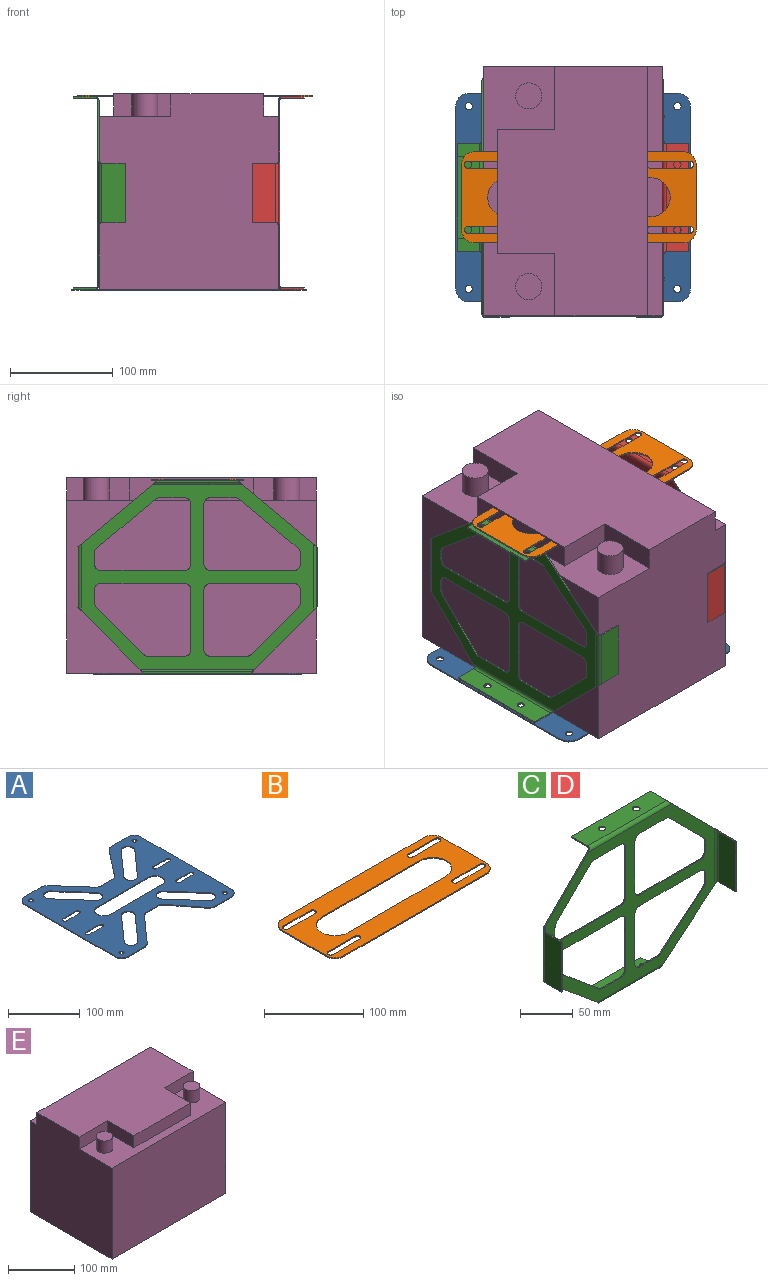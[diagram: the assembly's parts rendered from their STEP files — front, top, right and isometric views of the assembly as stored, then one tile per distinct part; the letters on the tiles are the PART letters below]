
ASSEMBLY  parts=5 mates=12
PART A: 66 faces, bbox 228.6x203.2x1.3 mm
  f0: plane 228.6x203.2mm, normal (0,0,1), area 27129.1mm2, adj f2,f3,f4,f5,f6,f7,f8,f9
  f1: plane 228.6x203.2mm, normal (0,0,-1), area 27129.1mm2, adj f2,f3,f4,f5,f6,f7,f8,f9
  f2: plane 31.89x1.27mm, normal (0,1,0), area 40.5mm2, adj f0,f1,f40,f45
  f3: plane 31.89x1.27mm, normal (0,-1,0), area 40.5mm2, adj f0,f1,f37,f44
  f4: plane 32.4x1.27mm, normal (0,1,0), area 41.1mm2, adj f0,f1,f39,f42
  f5: plane 177.8x1.27mm, normal (-1,0,0), area 225.8mm2, adj f0,f1,f42,f43
  f6: plane 32.4x1.27mm, normal (0,-1,0), area 41.1mm2, adj f0,f1,f36,f43
  f7: plane 177.8x1.27mm, normal (1,0,0), area 225.8mm2, adj f0,f1,f44,f45
  f8: cylinder r=3.57mm len=7.14mm, axis (0,0,1), area 14.2mm2, adj f0,f1,f9,f11
  f9: plane 25.4x1.27mm, normal (0,1,0), area 32.3mm2, adj f0,f1,f8,f10
  f10: cylinder r=3.57mm len=7.14mm, axis (0,0,1), area 14.2mm2, adj f0,f1,f9,f11
  f11: plane 25.4x1.27mm, normal (0,-1,0), area 32.3mm2, adj f0,f1,f8,f10
  f12: cylinder r=3.57mm len=7.14mm, axis (0,0,1), area 28.5mm2, adj f0,f1
  f13: cylinder r=3.57mm len=7.14mm, axis (0,0,1), area 28.5mm2, adj f0,f1
  f14: cylinder r=3.57mm len=7.14mm, axis (0,0,1), area 28.5mm2, adj f0,f1
  f15: cylinder r=3.57mm len=7.14mm, axis (0,0,1), area 14.2mm2, adj f0,f1,f16,f18
  f16: plane 25.4x1.27mm, normal (0,-1,0), area 32.3mm2, adj f0,f1,f15,f17
  f17: cylinder r=3.57mm len=7.14mm, axis (0,0,1), area 14.2mm2, adj f0,f1,f16,f18
  f18: plane 25.4x1.27mm, normal (0,1,0), area 32.3mm2, adj f0,f1,f15,f17
  f19: cylinder r=3.57mm len=7.14mm, axis (0,0,1), area 14.2mm2, adj f0,f1,f20,f22
  f20: plane 25.4x1.27mm, normal (0,1,0), area 32.3mm2, adj f0,f1,f19,f21
  f21: cylinder r=3.57mm len=7.14mm, axis (0,0,1), area 14.2mm2, adj f0,f1,f20,f22
  f22: plane 25.4x1.27mm, normal (0,-1,0), area 32.3mm2, adj f0,f1,f19,f21
  f23: plane 25.4x1.27mm, normal (0,1,0), area 32.3mm2, adj f0,f1,f24,f26
  f24: cylinder r=3.57mm len=7.14mm, axis (0,0,1), area 14.2mm2, adj f0,f1,f23,f25
  f25: plane 25.4x1.27mm, normal (0,-1,0), area 32.3mm2, adj f0,f1,f24,f26
  f26: cylinder r=3.57mm len=7.14mm, axis (0,0,1), area 14.2mm2, adj f0,f1,f23,f25
  f27: cylinder r=3.57mm len=7.14mm, axis (0,0,1), area 28.5mm2, adj f0,f1
  f28: plane 47.34x36.82mm, normal (-0.79,-0.61,0), area 76.2mm2, adj f0,f1,f34,f37
  f29: plane 19.84x1.27mm, normal (0,-1,0), area 25.2mm2, adj f0,f1,f34,f35
  f30: plane 48.63x43.22mm, normal (0.75,-0.66,0), area 82.6mm2, adj f0,f1,f35,f36
  f31: plane 19.84x1.27mm, normal (0,1,0), area 25.2mm2, adj f0,f1,f38,f41
  f32: plane 47.34x36.82mm, normal (-0.79,0.61,0), area 76.2mm2, adj f0,f1,f40,f41
  f33: plane 48.63x43.22mm, normal (0.75,0.66,0), area 82.6mm2, adj f0,f1,f38,f39
  f34: cylinder r=12.7mm len=10.02mm, axis (0,0,-1), area 14.7mm2, adj f0,f1,f28,f29
  f35: cylinder r=12.7mm len=9.49mm, axis (0,0,1), area 13.6mm2, adj f0,f1,f29,f30
  f36: cylinder r=12.7mm len=9.49mm, axis (0,0,1), area 13.6mm2, adj f0,f1,f6,f30
  f37: cylinder r=12.7mm len=10.02mm, axis (0,0,-1), area 14.7mm2, adj f0,f1,f3,f28
  f38: cylinder r=12.7mm len=9.49mm, axis (0,0,1), area 13.6mm2, adj f0,f1,f31,f33
  f39: cylinder r=12.7mm len=9.49mm, axis (0,0,1), area 13.6mm2, adj f0,f1,f4,f33
  f40: cylinder r=12.7mm len=10.02mm, axis (0,0,-1), area 14.7mm2, adj f0,f1,f2,f32
  f41: cylinder r=12.7mm len=10.02mm, axis (0,0,-1), area 14.7mm2, adj f0,f1,f31,f32
  f42: cylinder r=12.7mm len=12.7mm, axis (0,0,-1), area 25.3mm2, adj f0,f1,f4,f5
  f43: cylinder r=12.7mm len=12.7mm, axis (0,0,1), area 25.3mm2, adj f0,f1,f5,f6
  f44: cylinder r=12.7mm len=12.7mm, axis (0,0,-1), area 25.3mm2, adj f0,f1,f3,f7
  f45: cylinder r=12.7mm len=12.7mm, axis (0,0,1), area 25.3mm2, adj f0,f1,f2,f7
  f46: plane 47.46x42.19mm, normal (0.75,0.66,0), area 80.6mm2, adj f0,f1,f47,f49
  f47: cylinder r=9.53mm len=16.64mm, axis (0,0,1), area 38mm2, adj f0,f1,f46,f48
  f48: plane 47.46x42.19mm, normal (-0.75,-0.66,0), area 80.6mm2, adj f0,f1,f47,f49
  f49: cylinder r=9.53mm len=16.64mm, axis (0,0,1), area 38mm2, adj f0,f1,f46,f48
  f50: cylinder r=12.7mm len=25.4mm, axis (0,0,1), area 50.7mm2, adj f0,f1,f51,f53
  f51: plane 101.6x1.27mm, normal (0,-1,0), area 129mm2, adj f0,f1,f50,f52
  f52: cylinder r=12.7mm len=25.4mm, axis (0,0,1), area 50.7mm2, adj f0,f1,f51,f53
  f53: plane 101.6x1.27mm, normal (0,1,0), area 129mm2, adj f0,f1,f50,f52
  f54: plane 47.46x42.19mm, normal (0.75,0.66,0), area 80.6mm2, adj f0,f1,f55,f57
  f55: cylinder r=9.53mm len=16.64mm, axis (0,0,1), area 38mm2, adj f0,f1,f54,f56
  f56: plane 47.46x42.19mm, normal (-0.75,-0.66,0), area 80.6mm2, adj f0,f1,f55,f57
  f57: cylinder r=9.53mm len=16.64mm, axis (0,0,1), area 38mm2, adj f0,f1,f54,f56
  f58: cylinder r=9.53mm len=16.64mm, axis (0,0,1), area 38mm2, adj f0,f1,f59,f61
  f59: plane 47.46x42.19mm, normal (0.75,-0.66,0), area 80.6mm2, adj f0,f1,f58,f60
  f60: cylinder r=9.53mm len=16.64mm, axis (0,0,1), area 38mm2, adj f0,f1,f59,f61
  f61: plane 47.46x42.19mm, normal (-0.75,0.66,0), area 80.6mm2, adj f0,f1,f58,f60
  f62: cylinder r=9.53mm len=16.64mm, axis (0,0,1), area 38mm2, adj f0,f1,f63,f65
  f63: plane 47.46x42.19mm, normal (-0.75,0.66,0), area 80.6mm2, adj f0,f1,f62,f64
  f64: cylinder r=9.53mm len=16.64mm, axis (0,0,1), area 38mm2, adj f0,f1,f63,f65
  f65: plane 47.46x42.19mm, normal (0.75,-0.66,0), area 80.6mm2, adj f0,f1,f62,f64
PART B: 30 faces, bbox 228.6x88.9x1.3 mm
  f0: plane 228.6x88.9mm, normal (0,0,1), area 12473.6mm2, adj f2,f3,f4,f5,f6,f7,f8,f9
  f1: plane 228.6x88.9mm, normal (0,0,-1), area 12473.6mm2, adj f2,f3,f4,f5,f6,f7,f8,f9
  f2: plane 203.2x1.27mm, normal (0,1,0), area 258.1mm2, adj f0,f1,f6,f9
  f3: plane 63.5x1.27mm, normal (-1,0,0), area 80.6mm2, adj f0,f1,f6,f7
  f4: plane 203.2x1.27mm, normal (0,-1,0), area 258.1mm2, adj f0,f1,f7,f8
  f5: plane 63.5x1.27mm, normal (1,0,0), area 80.6mm2, adj f0,f1,f8,f9
  f6: cylinder r=12.7mm len=12.7mm, axis (0,0,-1), area 25.3mm2, adj f0,f1,f2,f3
  f7: cylinder r=12.7mm len=12.7mm, axis (0,0,1), area 25.3mm2, adj f0,f1,f3,f4
  f8: cylinder r=12.7mm len=12.7mm, axis (0,0,-1), area 25.3mm2, adj f0,f1,f4,f5
  f9: cylinder r=12.7mm len=12.7mm, axis (0,0,1), area 25.3mm2, adj f0,f1,f2,f5
  f10: cylinder r=3.57mm len=7.14mm, axis (0,0,1), area 14.2mm2, adj f0,f1,f11,f13
  f11: plane 38.1x1.27mm, normal (0,1,0), area 48.4mm2, adj f0,f1,f10,f12
  f12: cylinder r=3.57mm len=7.14mm, axis (0,0,1), area 14.2mm2, adj f0,f1,f11,f13
  f13: plane 38.1x1.27mm, normal (0,-1,0), area 48.4mm2, adj f0,f1,f10,f12
  f14: plane 38.1x1.27mm, normal (0,-1,0), area 48.4mm2, adj f0,f1,f15,f17
  f15: cylinder r=3.57mm len=7.14mm, axis (0,0,1), area 14.2mm2, adj f0,f1,f14,f16
  f16: plane 38.1x1.27mm, normal (0,1,0), area 48.4mm2, adj f0,f1,f15,f17
  f17: cylinder r=3.57mm len=7.14mm, axis (0,0,1), area 14.2mm2, adj f0,f1,f14,f16
  f18: plane 38.1x1.27mm, normal (0,1,0), area 48.4mm2, adj f0,f1,f19,f21
  f19: cylinder r=3.57mm len=7.14mm, axis (0,0,1), area 14.2mm2, adj f0,f1,f18,f20
  f20: plane 38.1x1.27mm, normal (0,-1,0), area 48.4mm2, adj f0,f1,f19,f21
  f21: cylinder r=3.57mm len=7.14mm, axis (0,0,1), area 14.2mm2, adj f0,f1,f18,f20
  f22: plane 38.1x1.27mm, normal (0,-1,0), area 48.4mm2, adj f0,f1,f23,f25
  f23: cylinder r=3.57mm len=7.14mm, axis (0,0,1), area 14.2mm2, adj f0,f1,f22,f24
  f24: plane 38.1x1.27mm, normal (0,1,0), area 48.4mm2, adj f0,f1,f23,f25
  f25: cylinder r=3.57mm len=7.14mm, axis (0,0,1), area 14.2mm2, adj f0,f1,f22,f24
  f26: cylinder r=19.05mm len=38.1mm, axis (0,0,1), area 76mm2, adj f0,f1,f27,f29
  f27: plane 139.7x1.27mm, normal (0,-1,0), area 177.4mm2, adj f0,f1,f26,f28
  f28: cylinder r=19.05mm len=38.1mm, axis (0,0,1), area 76mm2, adj f0,f1,f27,f29
  f29: plane 139.7x1.27mm, normal (0,1,0), area 177.4mm2, adj f0,f1,f26,f28
PART C: 86 faces, bbox 233.7x50.8x187.3 mm
  f0: plane 57.15x57.15mm, normal (-0.71,0,0.71), area 102.6mm2, adj f44,f45,f60,f83
  f1: plane 69.34x57.79mm, normal (-0.64,0,-0.77), area 114.6mm2, adj f44,f45,f61,f71
  f2: plane 69.34x57.79mm, normal (0.64,0,-0.77), area 114.6mm2, adj f44,f45,f52,f72
  f3: cylinder r=6.35mm len=4.49mm, axis (0,-1,0), area 6.3mm2, adj f4,f42,f44,f45
  f4: plane 45.99x45.99mm, normal (0.71,0,-0.71), area 82.6mm2, adj f3,f5,f44,f45
  f5: cylinder r=6.35mm len=4.49mm, axis (0,-1,0), area 6.3mm2, adj f4,f6,f44,f45
  f6: plane 35.29x1.27mm, normal (0,0,-1), area 44.8mm2, adj f5,f7,f44,f45
  f7: cylinder r=6.35mm len=6.35mm, axis (0,-1,0), area 12.7mm2, adj f6,f8,f44,f45
  f8: plane 58.1x1.27mm, normal (-1,0,0), area 73.8mm2, adj f7,f9,f44,f45
  f9: cylinder r=6.35mm len=6.35mm, axis (0,-1,0), area 12.7mm2, adj f8,f10,f44,f45
  f10: plane 81.28x1.27mm, normal (0,0,1), area 103.2mm2, adj f9,f11,f44,f45
  f11: cylinder r=6.35mm len=6.35mm, axis (0,-1,0), area 12.7mm2, adj f10,f42,f44,f45
  f12: cylinder r=6.35mm len=6.35mm, axis (0,-1,0), area 12.7mm2, adj f13,f41,f44,f45
  f13: plane 35.29x1.27mm, normal (0,0,-1), area 44.8mm2, adj f12,f14,f44,f45
  f14: cylinder r=6.35mm len=4.49mm, axis (0,-1,0), area 6.3mm2, adj f13,f15,f44,f45
  f15: plane 45.99x45.99mm, normal (-0.71,0,-0.71), area 82.6mm2, adj f14,f16,f44,f45
  f16: cylinder r=6.35mm len=4.49mm, axis (0,-1,0), area 6.3mm2, adj f15,f17,f44,f45
  f17: plane 12.11x1.27mm, normal (-1,0,0), area 15.4mm2, adj f16,f18,f44,f45
  f18: cylinder r=6.35mm len=6.35mm, axis (0,-1,0), area 12.7mm2, adj f17,f19,f44,f45
  f19: plane 81.28x1.27mm, normal (0,0,1), area 103.2mm2, adj f18,f20,f44,f45
  f20: cylinder r=6.35mm len=6.35mm, axis (0,-1,0), area 12.7mm2, adj f19,f41,f44,f45
  f21: cylinder r=6.35mm len=6.35mm, axis (0,-1,0), area 12.7mm2, adj f22,f40,f44,f45
  f22: plane 58.1x1.27mm, normal (-1,0,0), area 73.8mm2, adj f21,f23,f44,f45
  f23: cylinder r=6.35mm len=6.35mm, axis (0,-1,0), area 12.7mm2, adj f22,f24,f44,f45
  f24: plane 24.09x1.27mm, normal (0,0,1), area 30.6mm2, adj f23,f25,f44,f45
  f25: cylinder r=6.35mm len=4.07mm, axis (0,-1,0), area 5.6mm2, adj f24,f26,f44,f45
  f26: plane 57.19x47.66mm, normal (0.64,0,0.77), area 94.5mm2, adj f25,f27,f44,f45
  f27: cylinder r=6.35mm len=4.88mm, axis (0,-1,0), area 7.1mm2, adj f26,f28,f44,f45
  f28: plane 10.45x1.27mm, normal (1,0,0), area 13.3mm2, adj f27,f29,f44,f45
  f29: cylinder r=6.35mm len=6.35mm, axis (0,-1,0), area 12.7mm2, adj f28,f40,f44,f45
  f30: cylinder r=6.35mm len=4.88mm, axis (0,-1,0), area 7.1mm2, adj f31,f39,f44,f45
  f31: plane 57.19x47.66mm, normal (-0.64,0,0.77), area 94.5mm2, adj f30,f32,f44,f45
  f32: cylinder r=6.35mm len=4.07mm, axis (0,-1,0), area 5.6mm2, adj f31,f33,f44,f45
  f33: plane 24.09x1.27mm, normal (0,0,1), area 30.6mm2, adj f32,f34,f44,f45
  f34: cylinder r=6.35mm len=6.35mm, axis (0,-1,0), area 12.7mm2, adj f33,f35,f44,f45
  f35: plane 58.1x1.27mm, normal (1,0,0), area 73.8mm2, adj f34,f36,f44,f45
  f36: cylinder r=6.35mm len=6.35mm, axis (0,-1,0), area 12.7mm2, adj f35,f37,f44,f45
  f37: plane 81.28x1.27mm, normal (0,0,-1), area 103.2mm2, adj f36,f38,f44,f45
  f38: cylinder r=6.35mm len=6.35mm, axis (0,-1,0), area 12.7mm2, adj f37,f39,f44,f45
  f39: plane 10.45x1.27mm, normal (-1,0,0), area 13.3mm2, adj f30,f38,f44,f45
  f40: plane 81.28x1.27mm, normal (0,0,-1), area 103.2mm2, adj f21,f29,f44,f45
  f41: plane 58.1x1.27mm, normal (1,0,0), area 73.8mm2, adj f12,f20,f44,f45
  f42: plane 12.11x1.27mm, normal (1,0,0), area 15.4mm2, adj f3,f11,f44,f45
  f43: plane 57.15x57.15mm, normal (0.71,0,0.71), area 102.6mm2, adj f44,f45,f51,f82
  f44: plane 226.06x179.71mm, normal (0,-1,0), area 12442.3mm2, adj f0,f1,f2,f3,f4,f5,f6,f7
  f45: plane 226.06x179.71mm, normal (0,1,0), area 12442.3mm2, adj f0,f1,f2,f3,f4,f5,f6,f7
  f46: plane 22.86x1.27mm, normal (0,0,-1), area 29mm2, adj f47,f49,f50,f52
  f47: plane 57.79x1.27mm, normal (0,-1,0), area 73.4mm2, adj f46,f48,f49,f50
  f48: plane 22.86x1.27mm, normal (0,0,1), area 29mm2, adj f47,f49,f50,f51
  f49: plane 57.79x22.86mm, normal (-1,0,0), area 1321mm2, adj f46,f47,f48,f54
  f50: plane 57.79x22.86mm, normal (1,0,0), area 1321mm2, adj f46,f47,f48,f53
  f51: bspline ~3.81x3.81mm, area 8.2mm2, adj f43,f48,f53,f54
  f52: bspline ~3.81x3.81mm, area 7.7mm2, adj f2,f46,f53,f54
  f53: cylinder r=3.81mm len=64.77mm, axis (0,0,1), area 361mm2, adj f45,f50,f51,f52
  f54: cylinder r=2.54mm len=64.77mm, axis (0,0,1), area 240.6mm2, adj f44,f49,f51,f52
  f55: plane 57.79x1.27mm, normal (0,-1,0), area 73.4mm2, adj f56,f57,f58,f59
  f56: plane 22.86x1.27mm, normal (0,0,-1), area 29mm2, adj f55,f58,f59,f61
  f57: plane 22.86x1.27mm, normal (0,0,1), area 29mm2, adj f55,f58,f59,f60
  f58: plane 57.79x22.86mm, normal (1,0,0), area 1321mm2, adj f55,f56,f57,f63
  f59: plane 57.79x22.86mm, normal (-1,0,0), area 1321mm2, adj f55,f56,f57,f62
  f60: bspline ~3.81x3.81mm, area 8.2mm2, adj f0,f57,f62,f63
  f61: bspline ~3.81x3.81mm, area 7.7mm2, adj f1,f56,f62,f63
  f62: cylinder r=3.81mm len=64.77mm, axis (0,0,1), area 361mm2, adj f45,f59,f60,f61
  f63: cylinder r=2.54mm len=64.77mm, axis (0,0,1), area 240.7mm2, adj f44,f58,f60,f61
  f64: plane 21.59x1.27mm, normal (1,0,0), area 27.4mm2, adj f68,f69,f70,f72
  f65: plane 21.59x1.27mm, normal (-1,0,0), area 27.4mm2, adj f68,f69,f70,f71
  f66: cylinder r=3.57mm len=7.14mm, axis (0,0,-1), area 28.5mm2, adj f69,f70
  f67: cylinder r=3.57mm len=7.14mm, axis (0,0,-1), area 28.5mm2, adj f69,f70
  f68: plane 79.76x1.27mm, normal (0,1,0), area 101.3mm2, adj f64,f65,f69,f70
  f69: plane 79.76x21.59mm, normal (0,0,-1), area 1641.9mm2, adj f64,f65,f66,f67,f68,f73
  f70: plane 79.76x21.59mm, normal (0,0,1), area 1641.9mm2, adj f64,f65,f66,f67,f68,f74
  f71: bspline ~3.84x3.81mm, area 8.3mm2, adj f1,f65,f73,f74
  f72: bspline ~3.83x3.81mm, area 8.3mm2, adj f2,f64,f73,f74
  f73: cylinder r=3.81mm len=87.38mm, axis (-1,0,0), area 493.1mm2, adj f44,f69,f71,f72
  f74: cylinder r=2.54mm len=87.38mm, axis (-1,0,0), area 328.7mm2, adj f45,f70,f71,f72
  f75: plane 21.59x1.27mm, normal (-1,0,0), area 27.4mm2, adj f79,f80,f81,f83
  f76: plane 21.59x1.27mm, normal (1,0,0), area 27.4mm2, adj f79,f80,f81,f82
  f77: cylinder r=3.57mm len=7.14mm, axis (0,0,1), area 28.5mm2, adj f80,f81
  f78: cylinder r=3.57mm len=7.14mm, axis (0,0,1), area 28.5mm2, adj f80,f81
  f79: plane 105.41x1.27mm, normal (0,1,0), area 133.9mm2, adj f75,f76,f80,f81
  f80: plane 105.41x21.59mm, normal (0,0,1), area 2195.8mm2, adj f75,f76,f77,f78,f79,f84
  f81: plane 105.41x21.59mm, normal (0,0,-1), area 2195.8mm2, adj f75,f76,f77,f78,f79,f85
  f82: bspline ~3.81x3.81mm, area 7.8mm2, adj f43,f76,f84,f85
  f83: bspline ~3.81x3.81mm, area 7.8mm2, adj f0,f75,f84,f85
  f84: cylinder r=3.81mm len=111.76mm, axis (1,0,0), area 643.9mm2, adj f44,f80,f82,f83
  f85: cylinder r=2.54mm len=111.76mm, axis (1,0,0), area 429.2mm2, adj f45,f81,f82,f83
PART D: same geometry as C
PART E: 18 faces, bbox 242.9x174.6x190.5 mm
  f0: plane 242.89x69.85mm, normal (0,0,1), area 9248.7mm2, adj f3,f4,f5,f7,f9,f11,f12,f13
  f1: plane 242.89x14.29mm, normal (0,0,1), area 3470.3mm2, adj f2,f3,f5,f16
  f2: plane 242.89x168.28mm, normal (0,1,0), area 40871.9mm2, adj f1,f3,f5,f6
  f3: plane 190.5x174.63mm, normal (-1,0,0), area 31396.1mm2, adj f0,f1,f2,f4,f6,f11,f16,f17
  f4: plane 242.89x168.28mm, normal (0,-1,0), area 40871.9mm2, adj f0,f3,f5,f6
  f5: plane 190.5x174.63mm, normal (1,0,0), area 31396.1mm2, adj f0,f1,f2,f4,f6,f15,f16,f17
  f6: plane 242.89x174.63mm, normal (0,0,-1), area 42414.2mm2, adj f2,f3,f4,f5
  f7: cylinder r=12.7mm len=25.4mm, axis (0,0,-1), area 1773.5mm2, adj f0,f8
  f8: plane 25.4x25.4mm, normal (0,0,1), area 506.7mm2, adj f7
  f9: cylinder r=12.7mm len=25.4mm, axis (0,0,-1), area 1773.5mm2, adj f0,f10
  f10: plane 25.4x25.4mm, normal (0,0,1), area 506.7mm2, adj f9
  f11: plane 61.12x22.23mm, normal (0,-1,0), area 1358.4mm2, adj f0,f3,f12,f17
  f12: plane 55.56x22.23mm, normal (-1,0,0), area 1234.9mm2, adj f0,f11,f13,f17
  f13: plane 120.65x22.23mm, normal (0,-1,0), area 2681.4mm2, adj f0,f12,f14,f17
  f14: plane 55.56x22.23mm, normal (1,0,0), area 1234.9mm2, adj f0,f13,f15,f17
  f15: plane 61.12x22.23mm, normal (0,-1,0), area 1358.4mm2, adj f0,f5,f14,f17
  f16: plane 242.89x22.23mm, normal (0,1,0), area 5398.2mm2, adj f1,f3,f5,f17
  f17: plane 242.89x146.05mm, normal (0,0,1), area 28681.9mm2, adj f3,f5,f11,f12,f13,f14,f15,f16
PLACE A t=(-2.59,-48.95,38.87)mm fixed
PLACE B t=(3.13,8.2,227.46)mm
PLACE C rot(axis=(0.71,-0.71,0),180deg) t=(49.48,168.22,226.19)mm
PLACE D rot(axis=(0.71,0.71,0),180deg) t=(173.31,-62.92,226.19)mm
PLACE E rot(axis=(0,0,-1),90deg) t=(24.08,179.96,40.14)mm
MATE cylindrical C.f66 <-> B.f10  axis (0,0,1) through (9.48,20.9,227.46)mm
MATE planar E.f4 <-> C.f44  axis (-1,0,0) through (24.08,58.52,124.27)mm
MATE cylindrical C.f67 <-> B.f15  axis (0,0,1) through (9.48,84.4,227.46)mm
MATE planar E.f2 <-> D.f44  axis (1,0,0) through (198.71,58.52,124.27)mm
MATE planar E.f6 <-> A.f0  axis (0,0,-1) through (111.4,58.52,40.14)mm
MATE planar D.f80 <-> A.f0  axis (0,0,-1) through (213.31,52.65,40.14)mm
MATE planar D.f69 <-> B.f1  axis (0,0,1) through (213.31,52.65,227.46)mm
MATE planar E.f5 <-> C.f49  axis (0,-1,0) through (113.18,-62.92,130.37)mm
MATE planar C.f80 <-> A.f0  axis (0,0,-1) through (20.27,52.65,40.14)mm
MATE planar C.f59 <-> D.f50  axis (0,1,0) through (38.05,169.49,133.8)mm
MATE cylindrical A.f24 <-> D.f77  axis (0,0,1) through (213.31,29.79,40.14)mm
MATE cylindrical D.f78 <-> A.f15  axis (0,0,1) through (213.31,75.51,41.41)mm
